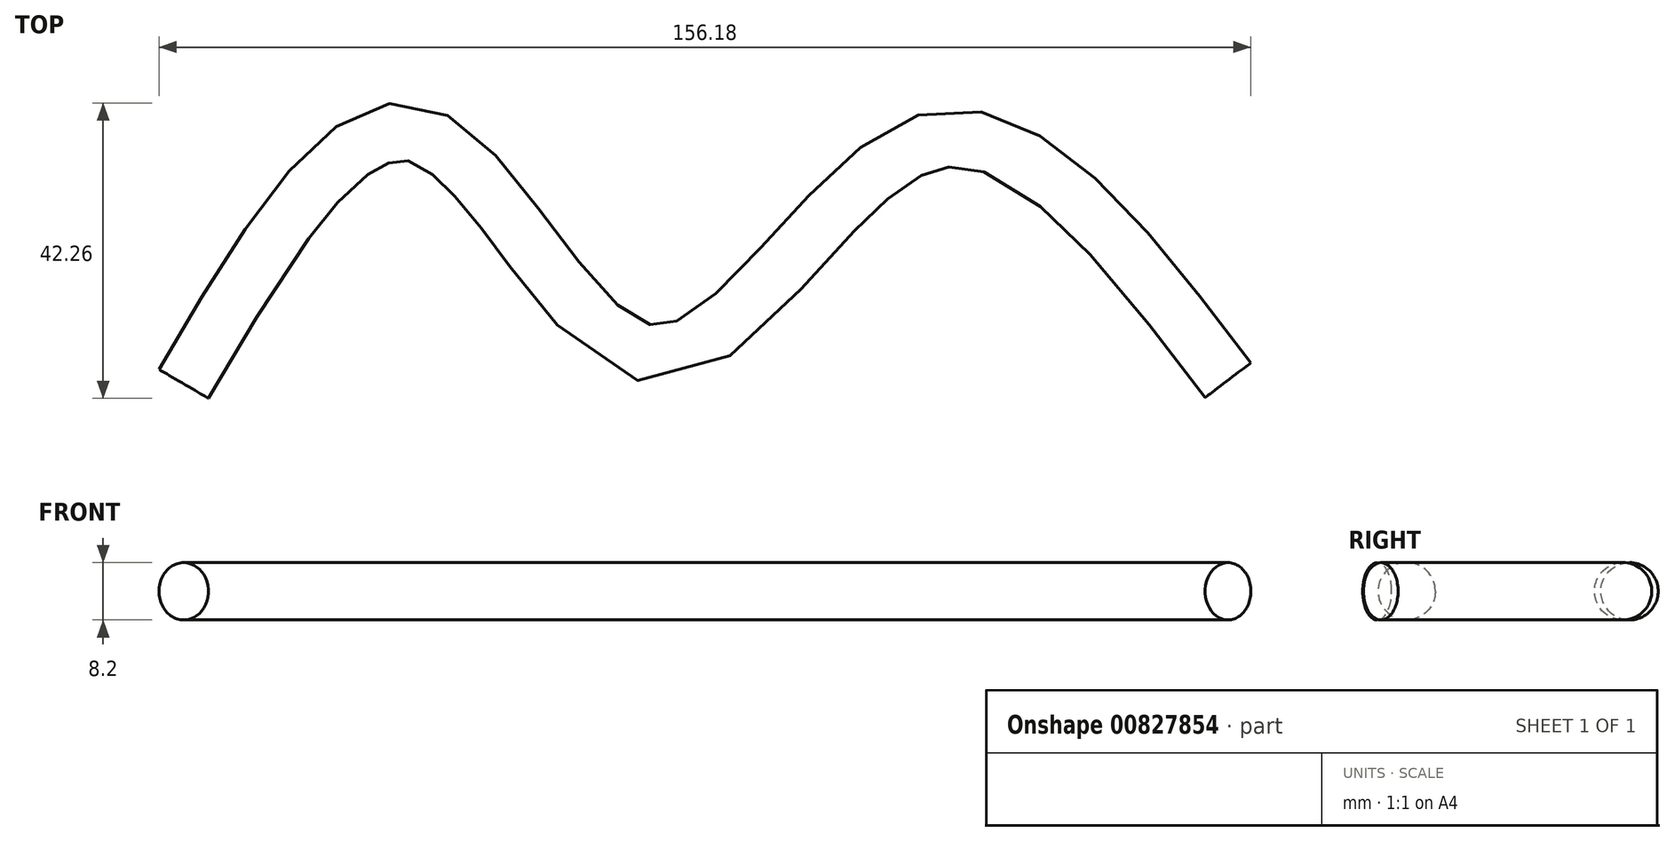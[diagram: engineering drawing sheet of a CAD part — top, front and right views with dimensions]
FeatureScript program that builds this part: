
annotation { "Feature Type Name" : "Feature", "Feature Type Description" : "" }
export const myFeature = defineFeature(function(context is Context, id is Id, definition is map)
    precondition{}
    {
        {
            var Q0;
            Q0=qCreatedBy(makeId("Top.planeOp"),FACE);
            var sketch = newSketch(context, id + "F0", { "sketchPlane" : qUnion([Q0])});
            skFitSpline(sketch, "E0", {"points": [v(-62.52, -14.37) * mm, v(-27.84, 21.29) * mm, v(4.94, -9.97) * mm, v(43.45, 20.15) * mm, v(87.36, -13.82) * mm], "startDerivative": vector(140.22, 239.88) * mm, "endDerivative": vector(168, -221.67) * mm});
            skSolve(sketch);
        }
        {
            var Q0;
            Q0=sQuery(id+"F0.wireOp",EDGE,"E0");
            var Q1;
            Q1=sQuery(id+"F0.wireOp",VERTEX,"E0.end");
            cPlane(context, id + "F1", {"entities" : qUnion([Q0, Q1]), "cplaneType" : CPlaneType.CURVE_POINT, "offset" : 25.4 * mm, "width" : 152.4 * mm, "height" : 152.4 * mm});
        }
        {
            var Q0;
            Q0=qCreatedBy(id+"F1.planeOp",FACE);
            var sketch = newSketch(context, id + "F2", { "sketchPlane" : qUnion([Q0])});
            skCircle(sketch, "E1", {"center": v(60.97, 0) * mm, "radius": 4.1 * mm});
            skSolve(sketch);
        }
        {
            var Q0;
            Q0=makeQuery(id+"F2.imprint","IMPRINT",FACE,{"disambiguationData":[TD([[makeQuery(id+"F2.imprint","IMPRINT",EDGE,{"derivedFrom":sQuery(id+"F2.wireOp",EDGE,"E1")}),1.0]])]});
            var Q1;
            Q1=sQuery(id+"F0.wireOp",EDGE,"E0");
            sweep(context, id + "F3", {"profiles" : qUnion([Q0]), "path" : qUnion([Q1])});
        }
    });
